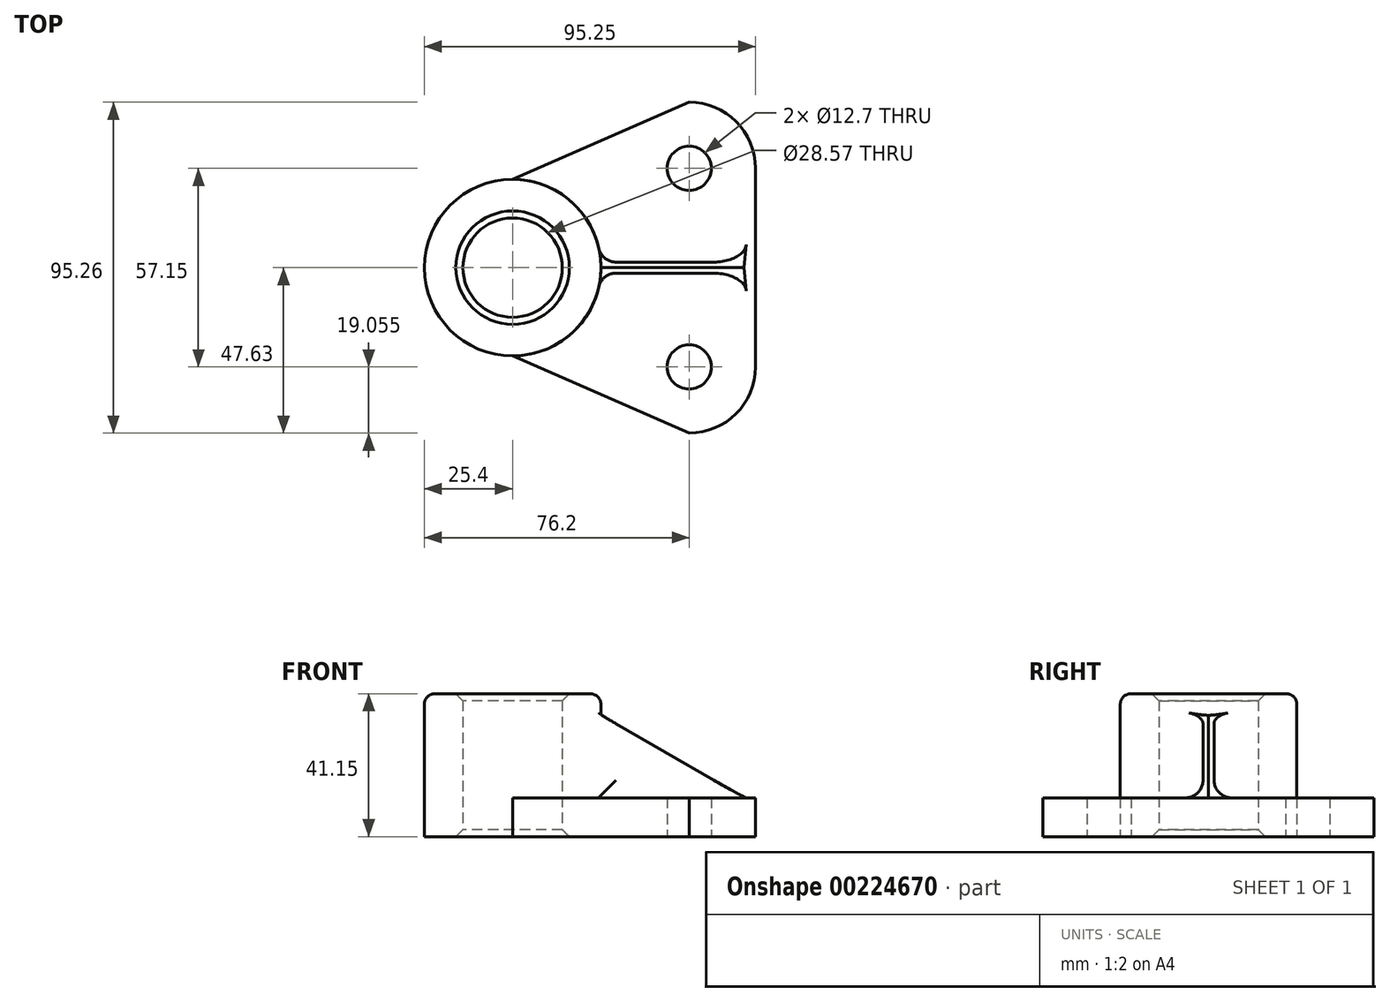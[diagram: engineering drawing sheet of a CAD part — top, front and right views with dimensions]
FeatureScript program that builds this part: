
annotation { "Feature Type Name" : "Feature", "Feature Type Description" : "" }
export const myFeature = defineFeature(function(context is Context, id is Id, definition is map)
    precondition{}
    {
        {
            var Q0;
            Q0=qCreatedBy(makeId("Top.planeOp"),FACE);
            var sketch = newSketch(context, id + "F0", { "sketchPlane" : qUnion([Q0])});
            skCircle(sketch, "E0", {"center": v(-50.8, 0) * mm, "radius": 25.4 * mm});
            skCircle(sketch, "E1", {"center": v(-50.8, 0) * mm, "radius": 14.29 * mm});
            skLineSegment(sketch, "E2", {"start": v(-50.8, 0) * mm, "end": v(19.05, 0) * mm, "construction": true});
            skCircle(sketch, "E3", {"center": v(0, -28.58) * mm, "radius": 6.35 * mm});
            skCircle(sketch, "E4", {"center": v(0, 28.58) * mm, "radius": 6.35 * mm});
            skLineSegment(sketch, "E5", {"start": v(19.05, -28.58) * mm, "end": v(19.05, 28.57) * mm});
            skArc(sketch, "E6", {"start": v(0, 47.62) * mm, "mid": v(13.47, 42.05) * mm, "end": v(19.05, 28.57) * mm});
            skArc(sketch, "E7", {"start": v(0, -47.62) * mm, "mid": v(13.47, -42.05) * mm, "end": v(19.05, -28.58) * mm});
            skPoint(sketch, "E8.start.orphan", {"position": v(-50.8, 25.4) * mm});
            skLineSegment(sketch, "E9", {"start": v(-50.8, -25.4) * mm, "end": v(0, -47.62) * mm});
            skLineSegment(sketch, "E10", {"start": v(-50.8, 25.4) * mm, "end": v(0, 47.62) * mm});
            skLineSegment(sketch, "E11", {"start": v(0, 47.62) * mm, "end": v(0, -47.62) * mm, "construction": true});
            skPoint(sketch, "E12.middle", {"position": v(-25.4, 0) * mm});
            skPoint(sketch, "E12.right.end.orphan", {"position": v(-33.16, 14.12) * mm});
            skPoint(sketch, "E13.orphan", {"position": v(-27.11, 12.18) * mm});
            skPoint(sketch, "E14.orphan", {"position": v(-17.64, -14.12) * mm});
            skPoint(sketch, "E12.left.end.orphan", {"position": v(-23.69, -12.18) * mm});
            skSolve(sketch);
        }
        {
            var Q0;
            Q0=makeQuery(id+"F0.imprint","IMPRINT",FACE,{"disambiguationData":[TD([[makeQuery(id+"F0.imprint","IMPRINT",EDGE,{"derivedFrom":sQuery(id+"F0.wireOp",EDGE,"E1")}),-1.0]])]});
            extrude(context, id + "F1", {"entities" : qUnion([Q0]), "depth" : 41.15 * mm});
        }
        {
            var Q0;
            Q0=makeQuery(id+"F0.imprint","IMPRINT",FACE,{"disambiguationData":[TD([[makeQuery(id+"F0.imprint","IMPRINT",EDGE,{"derivedFrom":sQuery(id+"F0.wireOp",EDGE,"E3")}),-1.0]])]});
            extrude(context, id + "F2", {"entities" : qUnion([Q0]), "operationType" : NewBodyOperationType.ADD, "depth" : 11.18 * mm});
        }
        {
            var Q0;
            Q0=makeQuery(id+"F1.opExtrude","CAP_EDGE",EDGE,{"disambiguationData":[OSD([sQuery(id+"F0.wireOp",EDGE,"E1")])],"isStart":false});
            chamfer(context, id + "F3", {"entities" : qUnion([Q0]), "chamferType" : ChamferType.OFFSET_ANGLE, "width" : 2.03 * mm, "oppositeDirection" : false, "angle" : 45 * degree, "tangentPropagation" : true});
        }
        {
            var Q0;
            Q0=makeQuery(id+"F1.opExtrude","CAP_EDGE",EDGE,{"disambiguationData":[OSD([sQuery(id+"F0.wireOp",EDGE,"E1")])],"isStart":true});
            chamfer(context, id + "F4", {"entities" : qUnion([Q0]), "chamferType" : ChamferType.OFFSET_ANGLE, "width" : 2.03 * mm, "oppositeDirection" : false, "angle" : 45 * degree, "tangentPropagation" : true});
        }
        {
            var Q0;
            Q0=qCreatedBy(makeId("Front.planeOp"),FACE);
            var sketch = newSketch(context, id + "F5", { "sketchPlane" : qUnion([Q0])});
            skLineSegment(sketch, "E15", {"start": v(-25.4, 34.93) * mm, "end": v(-25.4, 11.18) * mm});
            skLineSegment(sketch, "E16.0", {"start": v(-25.4, 11.18) * mm, "end": v(0, 11.18) * mm});
            skLineSegment(sketch, "E17.0", {"start": v(0, 11.18) * mm, "end": v(15.75, 11.18) * mm});
            skLineSegment(sketch, "E18", {"start": v(-25.4, 34.93) * mm, "end": v(15.75, 11.18) * mm});
            skPoint(sketch, "E19.orphan", {"position": v(19.05, 11.18) * mm});
            skPoint(sketch, "E20.orphan", {"position": v(-50.8, 11.18) * mm});
            skSolve(sketch);
        }
        {
            var Q0;
            Q0=makeQuery(id+"F5.imprint","IMPRINT",FACE,{"disambiguationData":[TD([[makeQuery(id+"F5.imprint","IMPRINT",EDGE,{"derivedFrom":sQuery(id+"F5.wireOp",EDGE,"E15")}),1.0]])]});
            extrude(context, id + "F6", {"entities" : qUnion([Q0]), "operationType" : NewBodyOperationType.ADD, "endBound" : BoundingType.SYMMETRIC, "depth" : 3.17 * mm, "hasDraft" : true, "draftAngle" : 3 * degree});
        }
        {
            var Q0;
            Q0=makeQuery(id+"F6.boolean.opBoolean","INTERSECT",EDGE,{"derivedFrom":[makeQuery(id+"F2.opExtrude","CAP_FACE",FACE,{"disambiguationData":[OSD([sQuery(id+"F0.wireOp",EDGE,"E0"),sQuery(id+"F0.wireOp",EDGE,"E3"),sQuery(id+"F0.wireOp",EDGE,"E4"),sQuery(id+"F0.wireOp",EDGE,"E5"),sQuery(id+"F0.wireOp",EDGE,"E6"),sQuery(id+"F0.wireOp",EDGE,"E7"),sQuery(id+"F0.wireOp",EDGE,"E9"),sQuery(id+"F0.wireOp",EDGE,"E10")])],"isStart":false}),makeQuery(id+"F6.opExtrude","CAP_FACE",FACE,{"disambiguationData":[OSD([sQuery(id+"F5.wireOp",EDGE,"E15"),sQuery(id+"F5.wireOp",EDGE,"E16.0"),sQuery(id+"F5.wireOp",EDGE,"E17.0"),sQuery(id+"F5.wireOp",EDGE,"E18")])],"isStart":true})]});
            var Q1;
            Q1=makeQuery(id+"F6.boolean.opBoolean","INTERSECT",EDGE,{"derivedFrom":[makeQuery(id+"F1.opExtrude","SWEPT_FACE",FACE,{"disambiguationData":[OSD([sQuery(id+"F0.wireOp",EDGE,"E0")])]}),makeQuery(id+"F6.opExtrude","CAP_FACE",FACE,{"disambiguationData":[OSD([sQuery(id+"F5.wireOp",EDGE,"E15"),sQuery(id+"F5.wireOp",EDGE,"E16.0"),sQuery(id+"F5.wireOp",EDGE,"E17.0"),sQuery(id+"F5.wireOp",EDGE,"E18")])],"isStart":true})]});
            var Q2;
            {var subQ0=sQuery(id+"F0.wireOp",EDGE,"E0");var subQ1=sQuery(id+"F0.wireOp",EDGE,"E10");Q2=makeQuery(id+"F6.boolean.opBoolean","SPLIT",EDGE,{"disambiguationData":[TD([makeQuery(id+"F2.opExtrude","SWEPT_FACE",FACE,{"disambiguationData":[OSD([subQ1])]})])],"derivedFrom":makeQuery(id+"F2.opExtrude","CAP_EDGE",EDGE,{"disambiguationData":[OSD([subQ0])],"isStart":false})});}
            fillet(context, id + "F7", {"entities" : qUnion([Q0, Q1, Q2]), "radius" : 5.08 * mm, "tangentPropagation" : true, "allowEdgeOverflow" : false});
        }
        {
            var Q0;
            Q0=makeQuery(id+"F6.boolean.opBoolean","INTERSECT",EDGE,{"derivedFrom":[makeQuery(id+"F1.opExtrude","SWEPT_FACE",FACE,{"disambiguationData":[OSD([sQuery(id+"F0.wireOp",EDGE,"E0")])]}),makeQuery(id+"F6.opExtrude","CAP_FACE",FACE,{"disambiguationData":[OSD([sQuery(id+"F5.wireOp",EDGE,"E15"),sQuery(id+"F5.wireOp",EDGE,"E16.0"),sQuery(id+"F5.wireOp",EDGE,"E17.0"),sQuery(id+"F5.wireOp",EDGE,"E18")])],"isStart":false})]});
            var Q1;
            {var subQ0=sQuery(id+"F0.wireOp",EDGE,"E0");var subQ1=sQuery(id+"F0.wireOp",EDGE,"E9");Q1=makeQuery(id+"F6.boolean.opBoolean","SPLIT",EDGE,{"disambiguationData":[TD([makeQuery(id+"F2.opExtrude","SWEPT_FACE",FACE,{"disambiguationData":[OSD([subQ1])]})])],"derivedFrom":makeQuery(id+"F2.opExtrude","CAP_EDGE",EDGE,{"disambiguationData":[OSD([subQ0])],"isStart":false})});}
            var Q2;
            Q2=makeQuery(id+"F6.boolean.opBoolean","INTERSECT",EDGE,{"derivedFrom":[makeQuery(id+"F2.opExtrude","CAP_FACE",FACE,{"disambiguationData":[OSD([sQuery(id+"F0.wireOp",EDGE,"E0"),sQuery(id+"F0.wireOp",EDGE,"E3"),sQuery(id+"F0.wireOp",EDGE,"E4"),sQuery(id+"F0.wireOp",EDGE,"E5"),sQuery(id+"F0.wireOp",EDGE,"E6"),sQuery(id+"F0.wireOp",EDGE,"E7"),sQuery(id+"F0.wireOp",EDGE,"E9"),sQuery(id+"F0.wireOp",EDGE,"E10")])],"isStart":false}),makeQuery(id+"F6.opExtrude","CAP_FACE",FACE,{"disambiguationData":[OSD([sQuery(id+"F5.wireOp",EDGE,"E15"),sQuery(id+"F5.wireOp",EDGE,"E16.0"),sQuery(id+"F5.wireOp",EDGE,"E17.0"),sQuery(id+"F5.wireOp",EDGE,"E18")])],"isStart":false})]});
            fillet(context, id + "F8", {"entities" : qUnion([Q0, Q1, Q2]), "radius" : 5.08 * mm, "tangentPropagation" : true, "allowEdgeOverflow" : false});
        }
        {
            var Q0;
            Q0=makeQuery(id+"F1.opExtrude","CAP_EDGE",EDGE,{"disambiguationData":[OSD([sQuery(id+"F0.wireOp",EDGE,"E0")])],"isStart":false});
            fillet(context, id + "F9", {"entities" : qUnion([Q0]), "radius" : 3.05 * mm, "tangentPropagation" : true, "allowEdgeOverflow" : false});
        }
    });
